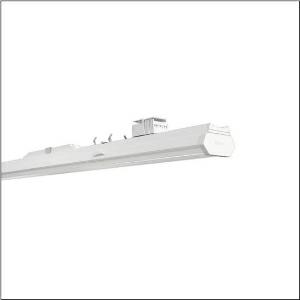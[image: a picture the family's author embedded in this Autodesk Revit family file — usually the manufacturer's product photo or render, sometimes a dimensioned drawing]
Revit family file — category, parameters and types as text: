
# Revit family: licross_21_protected_mo_52td12dn4a5g
name_source: partatom
category: Lighting Fixtures
units: mm (PartAtom-declared; Revit-internal decimal feet)

## family parameters
Cut with Voids When Loaded = No
Host = Face
Light Source = No
Part Type = Normal
Room Calculation Point = No
Round Connector Dimension = Use Diameter
Shared = No

## types (1)
- --- (1 x LED, 10700 lm, 62 W, 4000K)
    Apparent Load = 62 VA
    CIE Flux Codes = 73 92 98 99 100
    Color Rendering = 80
    Color Temperature = 4000K
    Default Elevation = 1800 mm
    Description = Licross 21 Protected MO, luminaire insert, of sheet steel, galvanised, coil coated, white, length: 1.500mm, width: 90mm, height: 103mm, LED rated luminous flux: 10.700lm, light colour: 840, SDCM (Standard Deviation of Colour Matching)MacAdam ≤ 3 SDCM (initial), control gear: DALI 2, with plug, 5-pole, with phase selection, mains connection: 220..240V, AC, 50/60Hz, rated input power: 62W, internal wiring halogen-free, primary light control with lens, of plastic, primary optical cover: cover, of PMMA, light emission: direct distribution, primary light characteristic: symmetric, protection rating (complete): IP54, insulation class (complete): insulation class I (protective earthing), certification: CE, ENEC, VDE, UKCA, protection symbol: D if used in an environment with non-conductive dust loads with corresponding accessories, impact resistance: IK06, permissible ambient temperature for indoor applications: -25..+35°C, corresponds to IFS (International Featured Standards) requirements for safety and quality in the food industry, reducing of maximum allowable ambient temperature of 5°C with ceiling mounting, LABS conformity tested according to VDMA 24364:2018-05, The light source and the operating device comply with the requirements of the Ecodesign Regulation (EU) 2019/2020 and are replaceable in accordance with this regulation, packaging unit: 1 piece
    Height = 92 mm
    Lamp = 1 x LED
    Lamp Light Flux = 10700 lm
    Lamp Power = 62 W
    Lamp count = 1
    Length = 1500 mm
    Luminous efficacy = 173 lm/W
    Manufacturer = Siteco
    ModVariant = No
    Model = 52TD12DN4A5G
    Mounting Place = Ceiling
    Mounting Type = Pendant
    Number of Poles = 1
    OnlyDefault = Yes
    Power Factor = 1
    Product Name = Licross 21 Protected MO
    Product group = luminaire insert | ceiling pendant
    ProductGroupID = 901
    Protection Class = Protection class I
    Protection Degree = IP 54
    RLX_Detail_Level = 1
    RLX_Emergency_Light_Flux = 0 lm
    RLX_Emergency_Type = 0
    RLX_Emergency_Type_DB = No
    RlxData = <blob elided: 24765 chars, md5=1e2d2c64>
    Socket = socket
    Standby Power = 0 W
    System Light Flux = 10700 lm
    System Power = 62 W
    Type Comments = factory setting: luminous flux: 100 % | dim-lin: 254 | 418 mA
    Type Image = l_1256148.jpg
    URL = http://relux.com
    VarID = @adj_128929
    Voltage = 0 V
    Weight = 0.00 kg
    Width = 88 mm

## geometry (parser evidence)
native form markers: Blend x4, Sweep x11
no freeform markers — native parametric forms only
